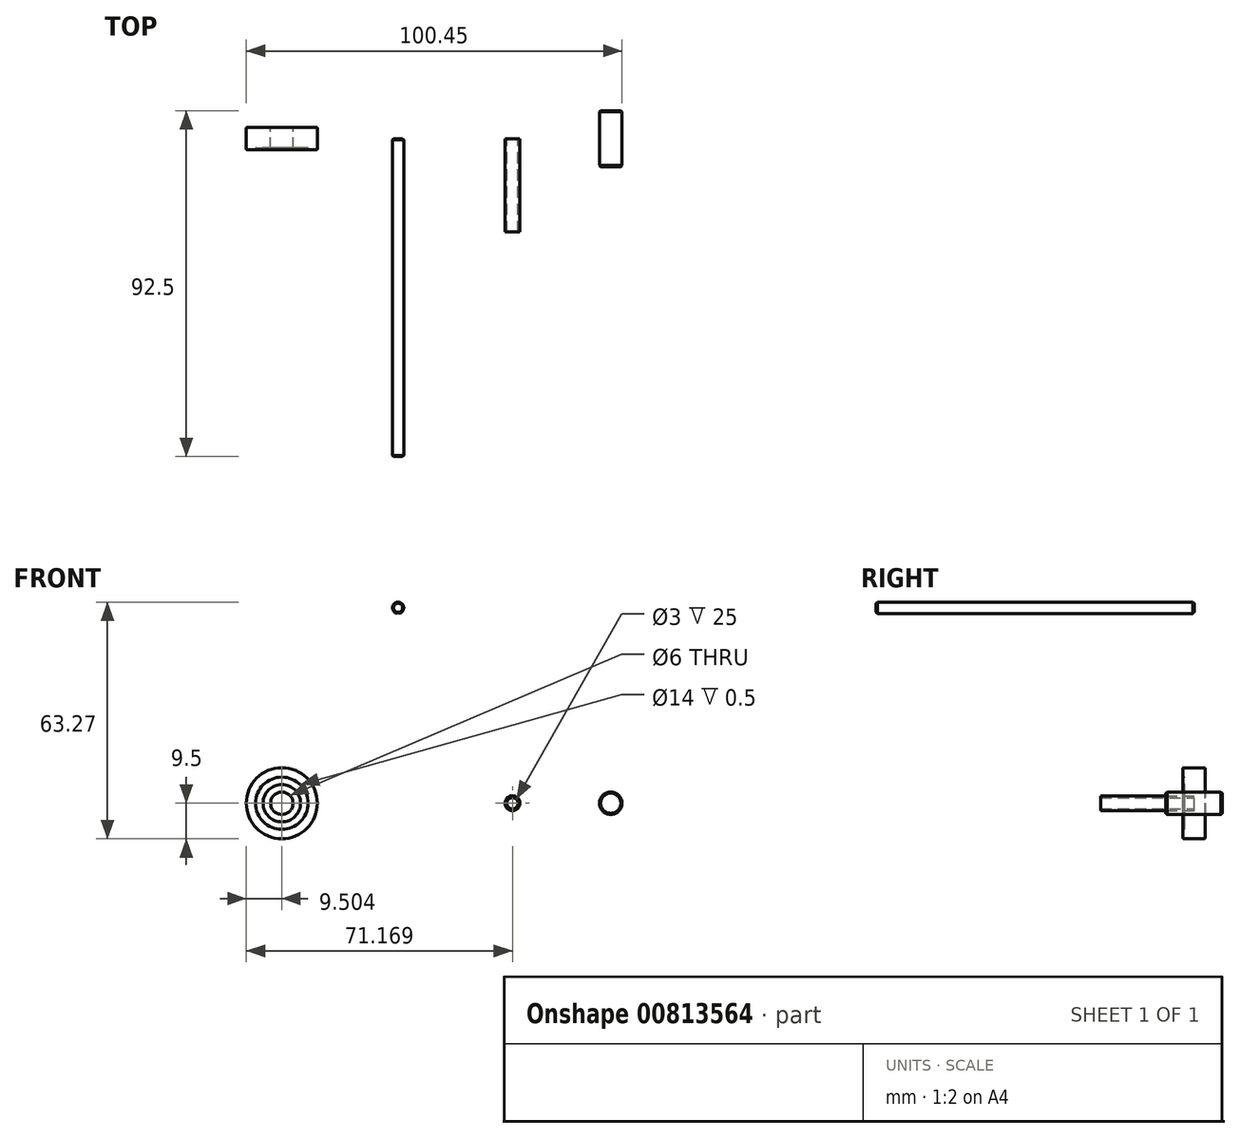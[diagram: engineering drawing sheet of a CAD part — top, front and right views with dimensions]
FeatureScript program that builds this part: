
annotation { "Feature Type Name" : "Feature", "Feature Type Description" : "" }
export const myFeature = defineFeature(function(context is Context, id is Id, definition is map)
    precondition{}
    {
        {
            var Q0;
            Q0=qCreatedBy(makeId("Front.planeOp"),FACE);
            var sketch = newSketch(context, id + "F0", { "sketchPlane" : qUnion([Q0])});
            skCircle(sketch, "E0", {"center": v(56.85, 0) * mm, "radius": 3 * mm});
            skSolve(sketch);
        }
        {
            var Q0;
            Q0=makeQuery(id+"F0.imprint","IMPRINT",FACE,{"disambiguationData":[TD([[makeQuery(id+"F0.imprint","IMPRINT",EDGE,{"derivedFrom":sQuery(id+"F0.wireOp",EDGE,"E0")}),1.0]])]});
            extrude(context, id + "F1", {"entities" : qUnion([Q0]), "endBound" : BoundingType.SYMMETRIC, "depth" : 15 * mm, "offsetDistance" : 25 * mm});
        }
        {
            var Q0;
            Q0=makeQuery(id+"F1.opExtrude","CAP_EDGE",EDGE,{"disambiguationData":[OSD([sQuery(id+"F0.wireOp",EDGE,"E0")])],"isStart":false});
            var Q1;
            Q1=makeQuery(id+"F1.opExtrude","CAP_EDGE",EDGE,{"disambiguationData":[OSD([sQuery(id+"F0.wireOp",EDGE,"E0")])],"isStart":true});
            chamfer(context, id + "F2", {"entities" : qUnion([Q0, Q1]), "width" : 0.3 * mm, "tangentPropagation" : true});
        }
        {
            var Q0;
            Q0=qCreatedBy(makeId("Front.planeOp"),FACE);
            var sketch = newSketch(context, id + "F3", { "sketchPlane" : qUnion([Q0])});
            skCircle(sketch, "E1", {"center": v(30.57, 0) * mm, "radius": 2 * mm});
            skCircle(sketch, "E2", {"center": v(30.57, 0) * mm, "radius": 1.5 * mm});
            skSolve(sketch);
        }
        {
            var Q0;
            Q0=makeQuery(id+"F3.imprint","IMPRINT",FACE,{"disambiguationData":[TD([[makeQuery(id+"F3.imprint","IMPRINT",EDGE,{"derivedFrom":sQuery(id+"F3.wireOp",EDGE,"E1")}),1.0]])]});
            extrude(context, id + "F4", {"entities" : qUnion([Q0]), "depth" : 25 * mm, "offsetDistance" : 25 * mm});
        }
        {
            var Q0;
            Q0=qCreatedBy(makeId("Front.planeOp"),FACE);
            var sketch = newSketch(context, id + "F5", { "sketchPlane" : qUnion([Q0])});
            skCircle(sketch, "E3", {"center": v(-31.1, 0) * mm, "radius": 3 * mm});
            skCircle(sketch, "E4", {"center": v(-31.1, 0) * mm, "radius": 9.5 * mm});
            skSolve(sketch);
        }
        {
            var Q0;
            Q0=makeQuery(id+"F5.imprint","IMPRINT",FACE,{"disambiguationData":[TD([[makeQuery(id+"F5.imprint","IMPRINT",EDGE,{"derivedFrom":sQuery(id+"F5.wireOp",EDGE,"E3")}),-1.0]])]});
            extrude(context, id + "F6", {"entities" : qUnion([Q0]), "endBound" : BoundingType.SYMMETRIC, "depth" : 6 * mm, "offsetDistance" : 25 * mm});
        }
        {
            var Q0;
            Q0=makeQuery(id+"F6.opExtrude","CAP_EDGE",EDGE,{"disambiguationData":[OSD([sQuery(id+"F5.wireOp",EDGE,"E4")])],"isStart":false});
            var Q1;
            Q1=makeQuery(id+"F6.opExtrude","CAP_EDGE",EDGE,{"disambiguationData":[OSD([sQuery(id+"F5.wireOp",EDGE,"E3")])],"isStart":false});
            var Q2;
            Q2=makeQuery(id+"F6.opExtrude","CAP_EDGE",EDGE,{"disambiguationData":[OSD([sQuery(id+"F5.wireOp",EDGE,"E3")])],"isStart":true});
            var Q3;
            Q3=makeQuery(id+"F6.opExtrude","CAP_EDGE",EDGE,{"disambiguationData":[OSD([sQuery(id+"F5.wireOp",EDGE,"E4")])],"isStart":true});
            fillet(context, id + "F7", {"entities" : qUnion([Q0, Q1, Q2, Q3]), "radius" : 0.3 * mm, "tangentPropagation" : true, "allowEdgeOverflow" : false});
        }
        {
            var Q0;
            Q0=makeQuery(id+"F6.opExtrude","CAP_FACE",FACE,{"disambiguationData":[OSD([sQuery(id+"F5.wireOp",EDGE,"E3"),sQuery(id+"F5.wireOp",EDGE,"E4")])],"isStart":false});
            var sketch = newSketch(context, id + "F8", { "sketchPlane" : qUnion([Q0])});
            skCircle(sketch, "E5", {"center": v(-31.1, 0) * mm, "radius": 5 * mm});
            skCircle(sketch, "E6", {"center": v(-31.1, 0) * mm, "radius": 7 * mm});
            skSolve(sketch);
        }
        {
            var Q0;
            Q0=makeQuery(id+"F8.imprint","IMPRINT",FACE,{"disambiguationData":[TD([[makeQuery(id+"F8.imprint","IMPRINT",EDGE,{"derivedFrom":sQuery(id+"F8.wireOp",EDGE,"E5")}),-1.0]])]});
            extrude(context, id + "F9", {"entities" : qUnion([Q0]), "operationType" : NewBodyOperationType.REMOVE, "oppositeDirection" : true, "depth" : 0.5 * mm, "offsetDistance" : 25 * mm});
        }
        {
            var Q0;
            {var subQ0=sQuery(id+"F5.wireOp",EDGE,"E3");Q0=makeQuery(id+"F7.opFillet","BLEND_EDGE",EDGE,{"blendedFrom":[makeQuery(id+"F6.opExtrude","CAP_EDGE",EDGE,{"disambiguationData":[OSD([subQ0])],"isStart":false}),makeQuery(id+"F6.opExtrude","CAP_FACE",FACE,{"disambiguationData":[OSD([subQ0,sQuery(id+"F5.wireOp",EDGE,"E4")])],"isStart":false})],"blendedInto":[makeQuery(id+"F6.opExtrude","CAP_FACE",FACE,{"disambiguationData":[OSD([subQ0,sQuery(id+"F5.wireOp",EDGE,"E4")])],"isStart":false})]});}
            var Q1;
            Q1=makeQuery(id+"F9.boolean.opBoolean","COPY",EDGE,{"derivedFrom":makeQuery(id+"F9.opExtrude","CAP_EDGE",EDGE,{"disambiguationData":[OSD([sQuery(id+"F8.wireOp",EDGE,"E5")])],"isStart":true})});
            var Q2;
            Q2=makeQuery(id+"F9.boolean.opBoolean","COPY",EDGE,{"derivedFrom":makeQuery(id+"F9.opExtrude","CAP_EDGE",EDGE,{"disambiguationData":[OSD([sQuery(id+"F8.wireOp",EDGE,"E6")])],"isStart":true})});
            var Q3;
            Q3=makeQuery(id+"FdbrrXm1rFhnAZ1_3.1.F9.boolean.opBoolean","COPY",EDGE,{"derivedFrom":makeQuery(id+"FdbrrXm1rFhnAZ1_3.1.F9.opExtrude","CAP_EDGE",EDGE,{"disambiguationData":[OSD([sQuery(id+"F8.wireOp",EDGE,"E5")])],"isStart":true})});
            var Q4;
            Q4=makeQuery(id+"FdbrrXm1rFhnAZ1_3.1.F9.boolean.opBoolean","COPY",EDGE,{"derivedFrom":makeQuery(id+"FdbrrXm1rFhnAZ1_3.1.F9.opExtrude","CAP_EDGE",EDGE,{"disambiguationData":[OSD([sQuery(id+"F8.wireOp",EDGE,"E6")])],"isStart":true})});
            fillet(context, id + "F10", {"entities" : qUnion([Q0, Q1, Q2, Q3, Q4]), "radius" : 0.3 * mm, "tangentPropagation" : true, "allowEdgeOverflow" : false});
        }
        {
            var Q0;
            Q0=qCreatedBy(makeId("Front.planeOp"),FACE);
            var sketch = newSketch(context, id + "F11", { "sketchPlane" : qUnion([Q0])});
            skCircle(sketch, "E7", {"center": v(0, 19.27) * mm, "radius": 1.5 * mm});
            skSolve(sketch);
        }
        {
            var Q0;
            Q0=makeQuery(id+"F11.imprint","IMPRINT",FACE,{"disambiguationData":[TD([[makeQuery(id+"F11.imprint","IMPRINT",EDGE,{"derivedFrom":sQuery(id+"F11.wireOp",EDGE,"E7")}),1.0]])]});
            extrude(context, id + "F12", {"entities" : qUnion([Q0]), "depth" : 85 * mm, "offsetDistance" : 25 * mm});
        }
        {
            var Q0;
            Q0=makeQuery(id+"F12.opExtrude","CAP_EDGE",EDGE,{"disambiguationData":[OSD([sQuery(id+"F11.wireOp",EDGE,"E7")])],"isStart":false});
            var Q1;
            Q1=makeQuery(id+"F12.opExtrude","CAP_EDGE",EDGE,{"disambiguationData":[OSD([sQuery(id+"F11.wireOp",EDGE,"E7")])],"isStart":true});
            chamfer(context, id + "F13", {"entities" : qUnion([Q0, Q1]), "width" : 0.3 * mm, "tangentPropagation" : true});
        }
        {
            var Q0;
            Q0=makeQuery(id+"F12.opExtrude","SWEPT_BODY",BODY,{"disambiguationData":[OSD([sQuery(id+"F11.wireOp",EDGE,"E7")])]});
            transform(context, id + "F14", {"entities" : qUnion([Q0]), "transformType" : TransformType.TRANSLATION_3D, "dx" : 0 * mm, "dy" : 0 * mm, "dz" : 33 * mm, "makeCopy" : false});
        }
    });
